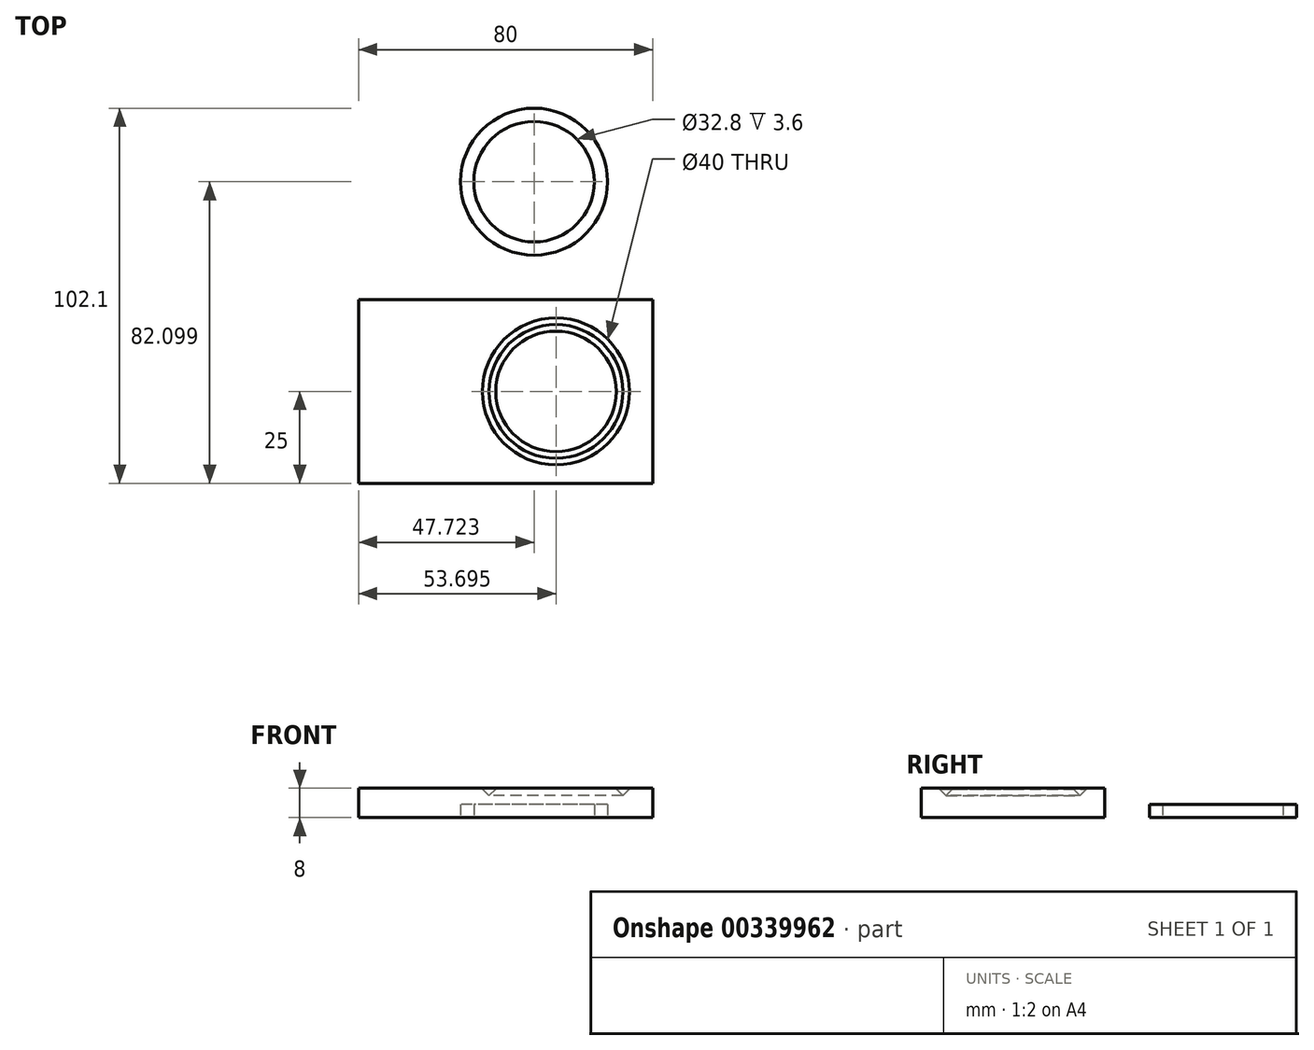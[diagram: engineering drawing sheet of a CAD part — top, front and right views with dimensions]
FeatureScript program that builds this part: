
annotation { "Feature Type Name" : "Feature", "Feature Type Description" : "" }
export const myFeature = defineFeature(function(context is Context, id is Id, definition is map)
    precondition{}
    {
        {
            var Q0;
            Q0=qCreatedBy(makeId("Top.planeOp"),FACE);
            var sketch = newSketch(context, id + "F0", { "sketchPlane" : qUnion([Q0])});
            skLineSegment(sketch, "E0.bottom", {"start": v(-40, 25) * mm, "end": v(40, 25) * mm});
            skLineSegment(sketch, "E0.top", {"start": v(-40, -25) * mm, "end": v(40, -25) * mm});
            skLineSegment(sketch, "E0.left", {"start": v(-40, 25) * mm, "end": v(-40, -25) * mm});
            skLineSegment(sketch, "E0.right", {"start": v(40, 25) * mm, "end": v(40, -25) * mm});
            skPoint(sketch, "E0.middle", {"position": v(0, 0) * mm});
            skSolve(sketch);
        }
        {
            var Q0;
            Q0 = qSketchRegion(id + "F0", true);
            extrude(context, id + "F1", {"entities" : qUnion([Q0]), "depth" : 8 * mm, "offsetDistance" : 25 * mm});
        }
        {
            var Q0;
            Q0=qCreatedBy(makeId("Top.planeOp"),FACE);
            var sketch = newSketch(context, id + "F2", { "sketchPlane" : qUnion([Q0])});
            skCircle(sketch, "E1", {"center": v(7.72, 57.1) * mm, "radius": 20 * mm});
            skCircle(sketch, "E2", {"center": v(7.72, 57.1) * mm, "radius": 16.4 * mm});
            skSolve(sketch);
        }
        {
            var Q0;
            Q0 = qSketchRegion(id + "F2", true);
            extrude(context, id + "F3", {"entities" : qUnion([Q0]), "depth" : 3.6 * mm, "offsetDistance" : 25 * mm});
        }
        {
            var Q0;
            Q0=makeQuery(id+"F1.opExtrude","CAP_FACE",FACE,{"disambiguationData":[OSD([sQuery(id+"F0.wireOp",EDGE,"E0.bottom"),sQuery(id+"F0.wireOp",EDGE,"E0.top"),sQuery(id+"F0.wireOp",EDGE,"E0.left"),sQuery(id+"F0.wireOp",EDGE,"E0.right")])],"isStart":false});
            var sketch = newSketch(context, id + "F4", { "sketchPlane" : qUnion([Q0])});
            skCircle(sketch, "E3", {"center": v(13.7, 0) * mm, "radius": 20 * mm});
            skCircle(sketch, "E4", {"center": v(13.7, 0) * mm, "radius": 16.4 * mm});
            skSolve(sketch);
        }
        {
            var Q0;
            Q0 = qSketchRegion(id + "F4", true);
            extrude(context, id + "F5", {"entities" : qUnion([Q0]), "operationType" : NewBodyOperationType.REMOVE, "oppositeDirection" : true, "depth" : 2 * mm, "offsetDistance" : 25 * mm});
        }
        {
            var Q0;
            Q0=makeQuery(id+"F5.boolean.opBoolean","COPY",EDGE,{"derivedFrom":makeQuery(id+"F5.opExtrude","CAP_EDGE",EDGE,{"disambiguationData":[OSD([sQuery(id+"F4.wireOp",EDGE,"E3")])],"isStart":false})});
            var Q1;
            Q1=makeQuery(id+"F5.boolean.opBoolean","COPY",EDGE,{"derivedFrom":makeQuery(id+"F5.opExtrude","CAP_EDGE",EDGE,{"disambiguationData":[OSD([sQuery(id+"F4.wireOp",EDGE,"E4")])],"isStart":false})});
            chamfer(context, id + "F6", {"entities" : qUnion([Q0, Q1]), "width" : 1.8 * mm, "tangentPropagation" : true});
        }
    });
